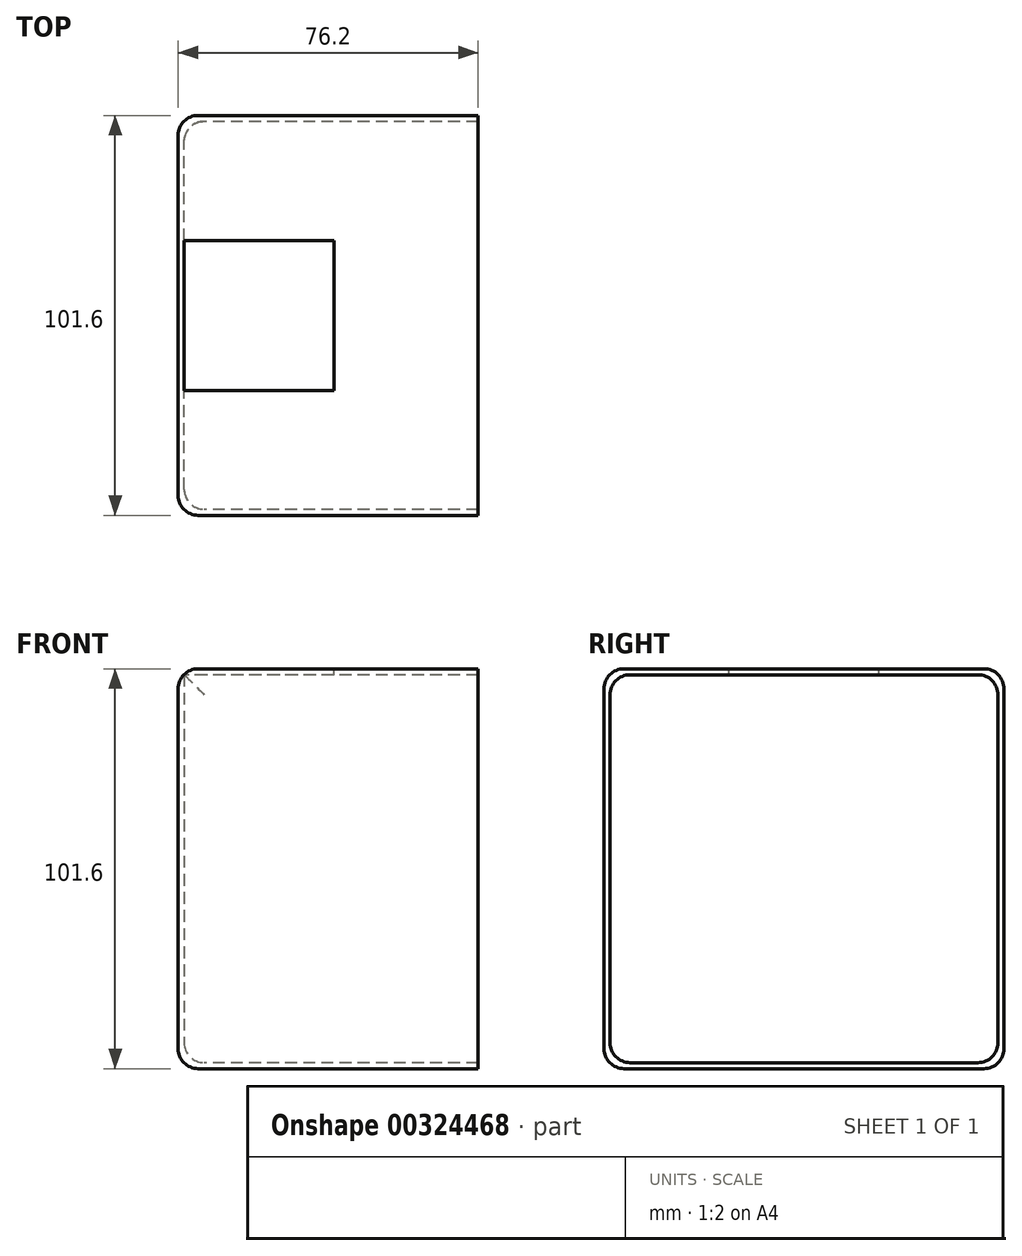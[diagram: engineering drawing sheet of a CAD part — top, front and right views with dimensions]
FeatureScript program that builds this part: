
annotation { "Feature Type Name" : "Feature", "Feature Type Description" : "" }
export const myFeature = defineFeature(function(context is Context, id is Id, definition is map)
    precondition{}
    {
        {
            var Q0;
            Q0=qCreatedBy(makeId("Right.planeOp"),FACE);
            var sketch = newSketch(context, id + "F0", { "sketchPlane" : qUnion([Q0])});
            skLineSegment(sketch, "E0.bottom", {"start": v(50.8, 50.8) * mm, "end": v(-50.8, 50.8) * mm});
            skLineSegment(sketch, "E0.top", {"start": v(50.8, -50.8) * mm, "end": v(-50.8, -50.8) * mm});
            skLineSegment(sketch, "E0.left", {"start": v(50.8, 50.8) * mm, "end": v(50.8, -50.8) * mm});
            skLineSegment(sketch, "E0.right", {"start": v(-50.8, 50.8) * mm, "end": v(-50.8, -50.8) * mm});
            skPoint(sketch, "E0.middle", {"position": v(0, 0) * mm});
            skLineSegment(sketch, "E1.bottom", {"start": v(-49.28, 49.28) * mm, "end": v(49.28, 49.28) * mm});
            skLineSegment(sketch, "E1.top", {"start": v(-49.28, -49.28) * mm, "end": v(49.28, -49.28) * mm});
            skLineSegment(sketch, "E1.left", {"start": v(-49.28, 49.28) * mm, "end": v(-49.28, -49.28) * mm});
            skLineSegment(sketch, "E1.right", {"start": v(49.28, 49.28) * mm, "end": v(49.28, -49.28) * mm});
            skSolve(sketch);
        }
        {
            var Q0;
            Q0=makeQuery(id+"F0.imprint","IMPRINT",FACE,{"disambiguationData":[TD([[makeQuery(id+"F0.imprint","IMPRINT",EDGE,{"derivedFrom":sQuery(id+"F0.wireOp",EDGE,"E0.bottom")}),1.0]])]});
            extrude(context, id + "F1", {"entities" : qUnion([Q0]), "depth" : 76.2 * mm});
        }
        {
            var Q0;
            Q0=qCreatedBy(makeId("Right.planeOp"),FACE);
            var sketch = newSketch(context, id + "F2", { "sketchPlane" : qUnion([Q0])});
            skLineSegment(sketch, "E2.bottom", {"start": v(50.8, 50.8) * mm, "end": v(-50.8, 50.8) * mm});
            skLineSegment(sketch, "E2.top", {"start": v(50.8, -50.8) * mm, "end": v(-50.8, -50.8) * mm});
            skLineSegment(sketch, "E2.left", {"start": v(50.8, 50.8) * mm, "end": v(50.8, -50.8) * mm});
            skLineSegment(sketch, "E2.right", {"start": v(-50.8, 50.8) * mm, "end": v(-50.8, -50.8) * mm});
            skPoint(sketch, "E2.middle", {"position": v(0, 0) * mm});
            skSolve(sketch);
        }
        {
            var Q0;
            Q0 = qSketchRegion(id + "F2", true);
            extrude(context, id + "F3", {"entities" : qUnion([Q0]), "operationType" : NewBodyOperationType.ADD, "depth" : 1.52 * mm});
        }
        {
            var Q0;
            Q0=makeQuery(id+"F1.opExtrude","SWEPT_FACE",FACE,{"disambiguationData":[OSD([sQuery(id+"F0.wireOp",EDGE,"E0.bottom")])]});
            var sketch = newSketch(context, id + "F4", { "sketchPlane" : qUnion([Q0])});
            skLineSegment(sketch, "E3.bottom", {"start": v(39.62, 19.05) * mm, "end": v(1.52, 19.05) * mm});
            skLineSegment(sketch, "E3.top", {"start": v(39.62, -19.05) * mm, "end": v(1.52, -19.05) * mm});
            skLineSegment(sketch, "E3.left", {"start": v(39.62, 19.05) * mm, "end": v(39.62, -19.05) * mm});
            skLineSegment(sketch, "E3.right", {"start": v(1.52, 19.05) * mm, "end": v(1.52, -19.05) * mm});
            skSolve(sketch);
        }
        {
            var Q0;
            Q0=makeQuery(id+"F4.imprint","IMPRINT",FACE,{"disambiguationData":[TD([[makeQuery(id+"F4.imprint","IMPRINT",EDGE,{"derivedFrom":sQuery(id+"F4.wireOp",EDGE,"E3.bottom")}),1.0]])]});
            extrude(context, id + "F5", {"entities" : qUnion([Q0]), "operationType" : NewBodyOperationType.REMOVE, "oppositeDirection" : true, "depth" : 1.52 * mm});
        }
        {
            var Q0;
            Q0=makeQuery(id+"F5.boolean.opBoolean","COPY",EDGE,{"derivedFrom":makeQuery(id+"F5.opExtrude","SWEPT_EDGE",EDGE,{"disambiguationData":[OSD([sQuery(id+"F4.wireOp",EDGE,"E3.bottom"),sQuery(id+"F4.wireOp",EDGE,"E3.left")])]})});
            var Q1;
            Q1=makeQuery(id+"F5.boolean.opBoolean","COPY",EDGE,{"derivedFrom":makeQuery(id+"F5.opExtrude","SWEPT_EDGE",EDGE,{"disambiguationData":[OSD([sQuery(id+"F4.wireOp",EDGE,"E3.top"),sQuery(id+"F4.wireOp",EDGE,"E3.left")])]})});
            var Q2;
            Q2=makeQuery(id+"F5.boolean.opBoolean","COPY",EDGE,{"derivedFrom":makeQuery(id+"F5.opExtrude","SWEPT_EDGE",EDGE,{"disambiguationData":[OSD([sQuery(id+"F4.wireOp",EDGE,"E3.top"),sQuery(id+"F4.wireOp",EDGE,"E3.right")])]})});
            var Q3;
            Q3=makeQuery(id+"F5.boolean.opBoolean","COPY",EDGE,{"derivedFrom":makeQuery(id+"F5.opExtrude","SWEPT_EDGE",EDGE,{"disambiguationData":[OSD([sQuery(id+"F4.wireOp",EDGE,"E3.bottom"),sQuery(id+"F4.wireOp",EDGE,"E3.right")])]})});
            fillet(context, id + "F6", {"entities" : qUnion([Q0, Q1, Q2, Q3]), "radius" : 5.08 * mm, "tangentPropagation" : true, "allowEdgeOverflow" : false});
        }
        {
            var Q0;
            Q0=makeQuery(id+"F1.opExtrude","SWEPT_EDGE",EDGE,{"disambiguationData":[OSD([sQuery(id+"F0.wireOp",EDGE,"E0.bottom"),sQuery(id+"F0.wireOp",EDGE,"E0.left")])]});
            var Q1;
            Q1=makeQuery(id+"F1.opExtrude","SWEPT_EDGE",EDGE,{"disambiguationData":[OSD([sQuery(id+"F0.wireOp",EDGE,"E0.bottom"),sQuery(id+"F0.wireOp",EDGE,"E0.right")])]});
            var Q2;
            Q2=makeQuery(id+"F1.opExtrude","SWEPT_EDGE",EDGE,{"disambiguationData":[OSD([sQuery(id+"F0.wireOp",EDGE,"E0.top"),sQuery(id+"F0.wireOp",EDGE,"E0.right")])]});
            var Q3;
            Q3=makeQuery(id+"F1.opExtrude","SWEPT_EDGE",EDGE,{"disambiguationData":[OSD([sQuery(id+"F0.wireOp",EDGE,"E0.top"),sQuery(id+"F0.wireOp",EDGE,"E0.left")])]});
            fillet(context, id + "F7", {"entities" : qUnion([Q0, Q1, Q2, Q3]), "radius" : 5.08 * mm, "tangentPropagation" : true, "allowEdgeOverflow" : false});
        }
        {
            var Q0;
            Q0=makeQuery(id+"F1.opExtrude","SWEPT_EDGE",EDGE,{"disambiguationData":[OSD([sQuery(id+"F0.wireOp",EDGE,"E1.top"),sQuery(id+"F0.wireOp",EDGE,"E1.left")])]});
            var Q1;
            Q1=makeQuery(id+"F1.opExtrude","SWEPT_EDGE",EDGE,{"disambiguationData":[OSD([sQuery(id+"F0.wireOp",EDGE,"E1.top"),sQuery(id+"F0.wireOp",EDGE,"E1.right")])]});
            var Q2;
            Q2=makeQuery(id+"F1.opExtrude","SWEPT_EDGE",EDGE,{"disambiguationData":[OSD([sQuery(id+"F0.wireOp",EDGE,"E1.bottom"),sQuery(id+"F0.wireOp",EDGE,"E1.right")])]});
            var Q3;
            Q3=makeQuery(id+"F1.opExtrude","SWEPT_EDGE",EDGE,{"disambiguationData":[OSD([sQuery(id+"F0.wireOp",EDGE,"E1.bottom"),sQuery(id+"F0.wireOp",EDGE,"E1.left")])]});
            fillet(context, id + "F8", {"entities" : qUnion([Q0, Q1, Q2, Q3]), "radius" : 5.08 * mm, "tangentPropagation" : true, "allowEdgeOverflow" : false});
        }
        {
            var Q0;
            Q0=makeQuery(id+"F3.boolean.opBoolean","MERGE",FACE,{"derivedFrom":[makeQuery(id+"F1.opExtrude","CAP_FACE",FACE,{"disambiguationData":[OSD([sQuery(id+"F0.wireOp",EDGE,"E0.bottom"),sQuery(id+"F0.wireOp",EDGE,"E0.top"),sQuery(id+"F0.wireOp",EDGE,"E0.left"),sQuery(id+"F0.wireOp",EDGE,"E0.right"),sQuery(id+"F0.wireOp",EDGE,"E1.bottom"),sQuery(id+"F0.wireOp",EDGE,"E1.top"),sQuery(id+"F0.wireOp",EDGE,"E1.left"),sQuery(id+"F0.wireOp",EDGE,"E1.right")])],"isStart":true}),makeQuery(id+"F3.opExtrude","CAP_FACE",FACE,{"disambiguationData":[OSD([sQuery(id+"F2.wireOp",EDGE,"E2.bottom"),sQuery(id+"F2.wireOp",EDGE,"E2.top"),sQuery(id+"F2.wireOp",EDGE,"E2.left"),sQuery(id+"F2.wireOp",EDGE,"E2.right")])],"isStart":true})]});
            fillet(context, id + "F9", {"entities" : qUnion([Q0]), "radius" : 5.08 * mm, "tangentPropagation" : true, "allowEdgeOverflow" : false});
        }
        {
            var Q0;
            Q0=makeQuery(id+"F3.boolean.opBoolean","INTERSECT",EDGE,{"derivedFrom":[makeQuery(id+"F1.opExtrude","SWEPT_FACE",FACE,{"disambiguationData":[OSD([sQuery(id+"F0.wireOp",EDGE,"E1.right")])]}),makeQuery(id+"F3.opExtrude","CAP_FACE",FACE,{"disambiguationData":[OSD([sQuery(id+"F2.wireOp",EDGE,"E2.bottom"),sQuery(id+"F2.wireOp",EDGE,"E2.top"),sQuery(id+"F2.wireOp",EDGE,"E2.left"),sQuery(id+"F2.wireOp",EDGE,"E2.right")])],"isStart":false})]});
            var Q1;
            Q1=makeQuery(id+"F3.boolean.opBoolean","INTERSECT",EDGE,{"derivedFrom":[makeQuery(id+"F1.opExtrude","SWEPT_FACE",FACE,{"disambiguationData":[OSD([sQuery(id+"F0.wireOp",EDGE,"E1.top")])]}),makeQuery(id+"F3.opExtrude","CAP_FACE",FACE,{"disambiguationData":[OSD([sQuery(id+"F2.wireOp",EDGE,"E2.bottom"),sQuery(id+"F2.wireOp",EDGE,"E2.top"),sQuery(id+"F2.wireOp",EDGE,"E2.left"),sQuery(id+"F2.wireOp",EDGE,"E2.right")])],"isStart":false})]});
            var Q2;
            Q2=makeQuery(id+"F3.boolean.opBoolean","INTERSECT",EDGE,{"derivedFrom":[makeQuery(id+"F1.opExtrude","SWEPT_FACE",FACE,{"disambiguationData":[OSD([sQuery(id+"F0.wireOp",EDGE,"E1.left")])]}),makeQuery(id+"F3.opExtrude","CAP_FACE",FACE,{"disambiguationData":[OSD([sQuery(id+"F2.wireOp",EDGE,"E2.bottom"),sQuery(id+"F2.wireOp",EDGE,"E2.top"),sQuery(id+"F2.wireOp",EDGE,"E2.left"),sQuery(id+"F2.wireOp",EDGE,"E2.right")])],"isStart":false})]});
            fillet(context, id + "F10", {"entities" : qUnion([Q0, Q1, Q2]), "radius" : 5.08 * mm, "allowEdgeOverflow" : false});
        }
        {
            var Q0;
            Q0=makeQuery(id+"F4.imprint","IMPRINT",FACE,{"disambiguationData":[TD([[makeQuery(id+"F4.imprint","IMPRINT",EDGE,{"derivedFrom":sQuery(id+"F4.wireOp",EDGE,"E3.bottom")}),1.0]])]});
            extrude(context, id + "F11", {"entities" : qUnion([Q0]), "operationType" : NewBodyOperationType.REMOVE, "oppositeDirection" : true, "depth" : 1.52 * mm});
        }
    });
